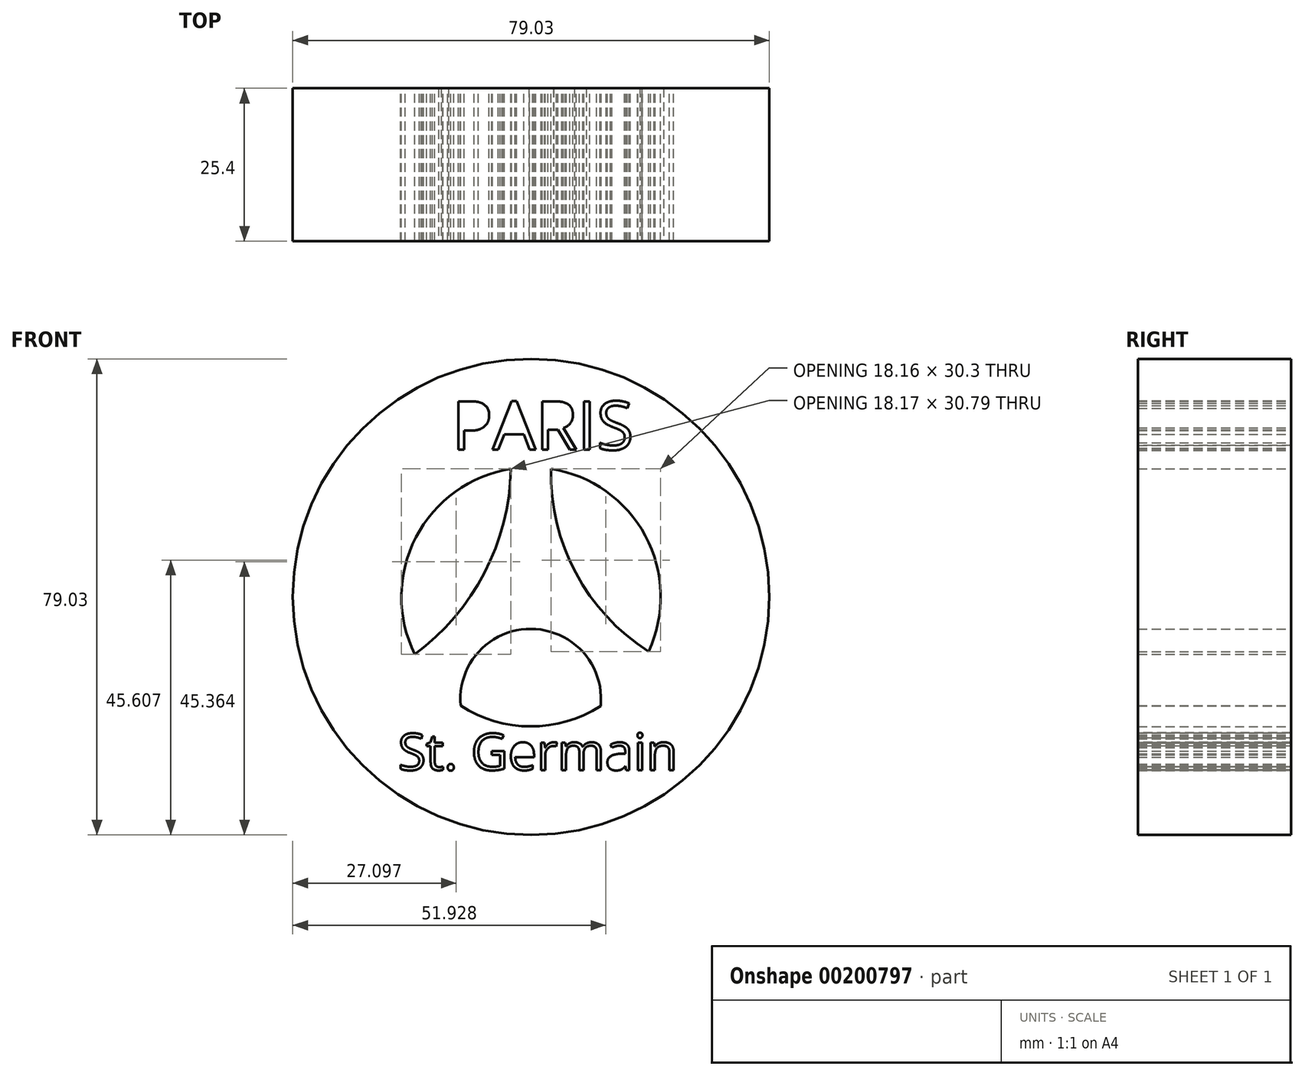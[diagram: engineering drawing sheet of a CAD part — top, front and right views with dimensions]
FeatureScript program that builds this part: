
annotation { "Feature Type Name" : "Feature", "Feature Type Description" : "" }
export const myFeature = defineFeature(function(context is Context, id is Id, definition is map)
    precondition{}
    {
        {
            var Q0;
            Q0=qCreatedBy(makeId("Front.planeOp"),FACE);
            var sketch = newSketch(context, id + "F0", { "sketchPlane" : qUnion([Q0])});
            skSolve(sketch);
        }
        {
            var Q0;
            Q0=qCreatedBy(makeId("Front.planeOp"),FACE);
            var sketch = newSketch(context, id + "F1", { "sketchPlane" : qUnion([Q0])});
            skCircle(sketch, "E0", {"center": v(6.87, 20.97) * mm, "radius": 39.52 * mm});
            skArc(sketch, "E1", {"start": v(-16.2, 21.97) * mm, "mid": v(7.25, -2.12) * mm, "end": v(29.9, 22.71) * mm});
            skArc(sketch, "E2", {"start": v(-10.95, 8.95) * mm, "mid": v(7, -0.53) * mm, "end": v(24.84, 9.15) * mm});
            skArc(sketch, "E3", {"start": v(-12.4, 11.43) * mm, "mid": v(-0.84, 24.97) * mm, "end": v(3.54, 42.22) * mm});
            skArc(sketch, "E4", {"start": v(-10.95, 8.95) * mm, "mid": v(0.64, 23.92) * mm, "end": v(4.84, 42.38) * mm});
            skArc(sketch, "E5", {"start": v(10.2, 42.22) * mm, "mid": v(14.3, 24.94) * mm, "end": v(26.38, 11.92) * mm});
            skArc(sketch, "E6", {"start": v(8.9, 42.38) * mm, "mid": v(12.8, 23.82) * mm, "end": v(24.84, 9.15) * mm});
            skLineSegment(sketch, "E7", {"start": v(-0.56, 21.57) * mm, "end": v(13.97, 21.57) * mm});
            skLineSegment(sketch, "E8", {"start": v(-1.16, 20.5) * mm, "end": v(13.97, 20.5) * mm});
            skArc(sketch, "E9", {"start": v(14.85, 1) * mm, "mid": v(6.85, 14.3) * mm, "end": v(-1.27, 1.07) * mm});
            skArc(sketch, "E10", {"start": v(18.43, 2.84) * mm, "mid": v(6.86, 15.66) * mm, "end": v(-4.8, 2.91) * mm});
            skArc(sketch, "E11.trimOffspring", {"start": v(26.38, 11.92) * mm, "mid": v(25.84, 31.1) * mm, "end": v(10.2, 42.22) * mm});
            skArc(sketch, "E12.trimOffspring", {"start": v(3.54, 42.22) * mm, "mid": v(-12.22, 30.86) * mm, "end": v(-12.4, 11.43) * mm});
            skArc(sketch, "E13.trimOffspring", {"start": v(8.9, 42.38) * mm, "mid": v(6.87, 42.48) * mm, "end": v(4.84, 42.38) * mm});
            skArc(sketch, "E14", {"start": v(-30.65, 21.97) * mm, "mid": v(7.24, -16.56) * mm, "end": v(44.37, 22.71) * mm});
            skLineSegment(sketch, "E15", {"start": v(-30.58, 23.45) * mm, "end": v(-16.09, 23.45) * mm});
            skLineSegment(sketch, "E16", {"start": v(-30.65, 21.97) * mm, "end": v(-16.2, 21.97) * mm});
            skLineSegment(sketch, "E17", {"start": v(29.8, 23.71) * mm, "end": v(44.31, 23.71) * mm});
            skLineSegment(sketch, "E18", {"start": v(29.9, 22.71) * mm, "end": v(44.37, 22.71) * mm});
            skPoint(sketch, "E18.startSnap0", {"position": v(29.9, 19.23) * mm});
            skArc(sketch, "E19.trimOffspring", {"start": v(29.8, 23.71) * mm, "mid": v(6.74, 44.07) * mm, "end": v(-16.09, 23.45) * mm});
            skArc(sketch, "E20.trimOffspring", {"start": v(44.31, 23.71) * mm, "mid": v(6.74, 58.51) * mm, "end": v(-30.58, 23.45) * mm});
            skText(sketch, "E21", { "text": "PARIS", "fontName": "OpenSans-Regular.ttf"});
            skText(sketch, "E22", { "text": "St. Germain", "fontName": "OpenSans-Regular.ttf"});
            const initialGuessF1  = {"E21": [-0.00626, 0.0454, 1, 0, 0.0081], "E22": [-0.0152, -0.00777, 1, 0, 0.0061]};
            skSetInitialGuess(sketch, initialGuessF1);
            skSolve(sketch);
        }
        {
            var Q0;
            Q0 = qSketchRegion(id + "F1", true);
            var Q1;
            {var subQ4=sQuery(id+"F1.wireOp",EDGE,"E3");Q1=makeQuery(id+"F1.imprint","IMPRINT",FACE,{"disambiguationData":[TD([[makeQuery(id+"F1.imprint","IMPRINT",EDGE,{"derivedFrom":subQ4}),-1.0]])]});}
            extrude(context, id + "F2", {"entities" : qUnion([Q0, Q1]), "depth" : 25.4 * mm});
        }
        {
            var Q0;
            Q0 = qSketchRegion(id + "F1", true);
            var Q1;
            Q1 = qSketchRegion(id + "F0", true);
            extrude(context, id + "F3", {"entities" : qUnion([Q0, Q1]), "operationType" : NewBodyOperationType.ADD, "depth" : 25.4 * mm});
        }
        {
            var Q0;
            Q0=makeQuery(id+"F1.imprint","IMPRINT",FACE,{"disambiguationData":[TD([[makeQuery(id+"F1.imprint","IMPRINT",EDGE,{"derivedFrom":sQuery(id+"F1.wireOp",EDGE,"E1")}),-1.0]])]});
            var Q1;
            Q1=makeQuery(id+"F1.imprint","IMPRINT",FACE,{"disambiguationData":[TD([[makeQuery(id+"F1.imprint","IMPRINT",EDGE,{"derivedFrom":sQuery(id+"F1.wireOp",EDGE,"E15")}),1.0]])]});
            var Q2;
            {var subQ2=sQuery(id+"F1.wireOp",EDGE,"E7");Q2=makeQuery(id+"F1.imprint","IMPRINT",FACE,{"disambiguationData":[TD([[makeQuery(id+"F1.imprint","IMPRINT",EDGE,{"derivedFrom":subQ2}),1.0]])]});}
            var Q3;
            {var subQ4=sQuery(id+"F1.wireOp",EDGE,"E7");Q3=makeQuery(id+"F1.imprint","IMPRINT",FACE,{"disambiguationData":[TD([[makeQuery(id+"F1.imprint","IMPRINT",EDGE,{"derivedFrom":subQ4}),-1.0]])]});}
            extrude(context, id + "F4", {"entities" : qUnion([Q0, Q1, Q2, Q3]), "operationType" : NewBodyOperationType.ADD, "depth" : 25.4 * mm});
        }
    });
